# Revit family: ВУТ_ВУЕ ВБ_Eng
name_source: partatom
category: Оборудование
units: mm (PartAtom-declared; Revit-internal decimal feet)

## family parameters
Всегда вертикально = Да
Классификация = Нет
На основе рабочей плоскости = Нет
Общий = Нет
При загрузке вырезать с полостями = Нет
Размер круглого соединителя = Использовать диаметр
Тип детали = Нормальный
Точка принадлежности помещению = Нет

## types (18) — shared parameters
00_20_Manufacturer = Vents
00_20_Name = Air handling units with heat recovery
Casing Material = Metal, painted, white, matte
Filter = G4, F7
Frequency = 50 Гц
Load Classification = HVAC
Maintenance zone material = <По категории>
Number of Fase = 1
URL = https://ventilation-system.com
Voltage = 230 В
Изготовитель = Vents
zero-valued in all types: Отметка по умолчанию

## per-type parameters (varying)
| type | Amperage | Apparent Load | B | D | Diameter | Dy | H | Height | L | Length | Maximum Air Flow | Power | Sound pressure level at 3 m distance | Weight | Width | b1 | h1 | l1 |
| VUT 160 V EC А21 | 1 А | 115 В·А | 330 мм | 125 мм | 125 мм | 115 мм | 550 мм | 600 мм | 600 мм | 600 мм | 200.0 м³/ч | 57 Вт | 24 dBA | 34.00 кг | 330 мм | 143 мм | 600 мм | 388 мм |
| VUT 550 VB EC А21 | 2 А | 552 В·А | 720 мм | 200 мм | 200 мм | 190 мм | 675 мм | 725 мм | 823 мм | 823 мм | 690.0 м³/ч | 337 Вт | 26 dBA | 82.00 кг | 720 мм | 284 мм | 725 мм | 493 мм |
| VUT 160 V1 EC А21 | 1 А | 115 В·А | 370 мм | 125 мм | 125 мм | 115 мм | 590 мм | 640 мм | 640 мм | 640 мм | 200.0 м³/ч | 57 Вт | 22 dBA | 42.00 кг | 370 мм | 143 мм | 640 мм | 388 мм |
| VUT 160 VB EC А21 | 1 А | 115 В·А | 330 мм | 125 мм | 125 мм | 115 мм | 580 мм | 630 мм | 600 мм | 600 мм | 200.0 м³/ч | 57 Вт | 24 dBA | 36.00 кг | 330 мм | 143 мм | 630 мм | 388 мм |
| VUT 160 V1B EC А21 | 1 А | 115 В·А | 370 мм | 125 мм | 125 мм | 115 мм | 620 мм | 670 мм | 640 мм | 640 мм | 200.0 м³/ч | 57 Вт | 22 dBA | 44.00 кг | 370 мм | 143 мм | 670 мм | 388 мм |
| VUT 250 V EC А21 | 1 А | 315 В·А | 560 мм | 160 мм | 160 мм | 150 мм | 970 мм | 1020 мм | 560 мм | 560 мм | 390.0 м³/ч | 180 Вт | 35 dBA | 66.00 кг | 560 мм | 212 мм | 1020 мм | 390 мм |
| VUT 250 VB EC А21 | 1 А | 315 В·А | 560 мм | 160 мм | 160 мм | 150 мм | 970 мм | 1020 мм | 560 мм | 560 мм | 390.0 м³/ч | 180 Вт | 35 dBA | 66.00 кг | 560 мм | 212 мм | 1020 мм | 390 мм |
| VUT 350 VB EC А21 | 1 А | 322 В·А | 583 мм | 160 мм | 160 мм | 150 мм | 675 мм | 725 мм | 730 мм | 730 мм | 450.0 м³/ч | 178 Вт | 28 dBA | 64.00 кг | 583 мм | 230 мм | 725 мм | 426 мм |
| VUT 350 V1B EC А21 | 1 А | 299 В·А | 470 мм | 160 мм | 160 мм | 150 мм | 675 мм | 725 мм | 730 мм | 730 мм | 420.0 м³/ч | 169 Вт | 28 dBA | 57.00 кг | 470 мм | 190 мм | 725 мм | 426 мм |
| VUE 160 V EC А21 | 1 А | 115 В·А | 330 мм | 125 мм | 125 мм | 115 мм | 550 мм | 600 мм | 600 мм | 600 мм | 200.0 м³/ч | 57 Вт | 24 dBA | 34.00 кг | 330 мм | 143 мм | 600 мм | 388 мм |
| VUE 160 V1 EC А21 | 1 А | 115 В·А | 370 мм | 125 мм | 125 мм | 115 мм | 590 мм | 640 мм | 640 мм | 640 мм | 200.0 м³/ч | 57 Вт | 22 dBA | 42.00 кг | 370 мм | 143 мм | 640 мм | 388 мм |
| VUE 160 V1B EC А21 | 1 А | 115 В·А | 370 мм | 125 мм | 125 мм | 115 мм | 620 мм | 670 мм | 640 мм | 640 мм | 200.0 м³/ч | 57 Вт | 22 dBA | 44.00 кг | 370 мм | 143 мм | 670 мм | 388 мм |
| VUE 160 VB EC А21 | 1 А | 115 В·А | 330 мм | 125 мм | 125 мм | 115 мм | 580 мм | 630 мм | 600 мм | 600 мм | 200.0 м³/ч | 57 Вт | 24 dBA | 36.00 кг | 330 мм | 143 мм | 630 мм | 388 мм |
| VUE 250 V EC А21 | 1 А | 315 В·А | 560 мм | 160 мм | 160 мм | 150 мм | 970 мм | 1020 мм | 560 мм | 560 мм | 390.0 м³/ч | 180 Вт | 35 dBA | 66.00 кг | 560 мм | 212 мм | 1020 мм | 390 мм |
| VUE 250 VB EC А21 | 1 А | 315 В·А | 560 мм | 160 мм | 160 мм | 150 мм | 970 мм | 1020 мм | 560 мм | 560 мм | 390.0 м³/ч | 180 Вт | 35 dBA | 66.00 кг | 560 мм | 212 мм | 1020 мм | 390 мм |
| VUE 350 V1B EC А21 | 1 А | 299 В·А | 470 мм | 160 мм | 160 мм | 150 мм | 675 мм | 725 мм | 730 мм | 730 мм | 420.0 м³/ч | 169 Вт | 28 dBA | 57.00 кг | 470 мм | 190 мм | 725 мм | 426 мм |
| VUE 350 VB EC А21 | 1 А | 322 В·А | 583 мм | 160 мм | 160 мм | 150 мм | 675 мм | 725 мм | 730 мм | 730 мм | 450.0 м³/ч | 178 Вт | 28 dBA | 64.00 кг | 583 мм | 230 мм | 725 мм | 426 мм |
| VUE 550 VB EC А21 | 2 А | 552 В·А | 720 мм | 200 мм | 200 мм | 190 мм | 675 мм | 725 мм | 823 мм | 823 мм | 690.0 м³/ч | 337 Вт | 26 dBA | 82.00 кг | 720 мм | 284 мм | 725 мм | 493 мм |

note: column(s) folded — value = type name in every type: 00_20_Type
